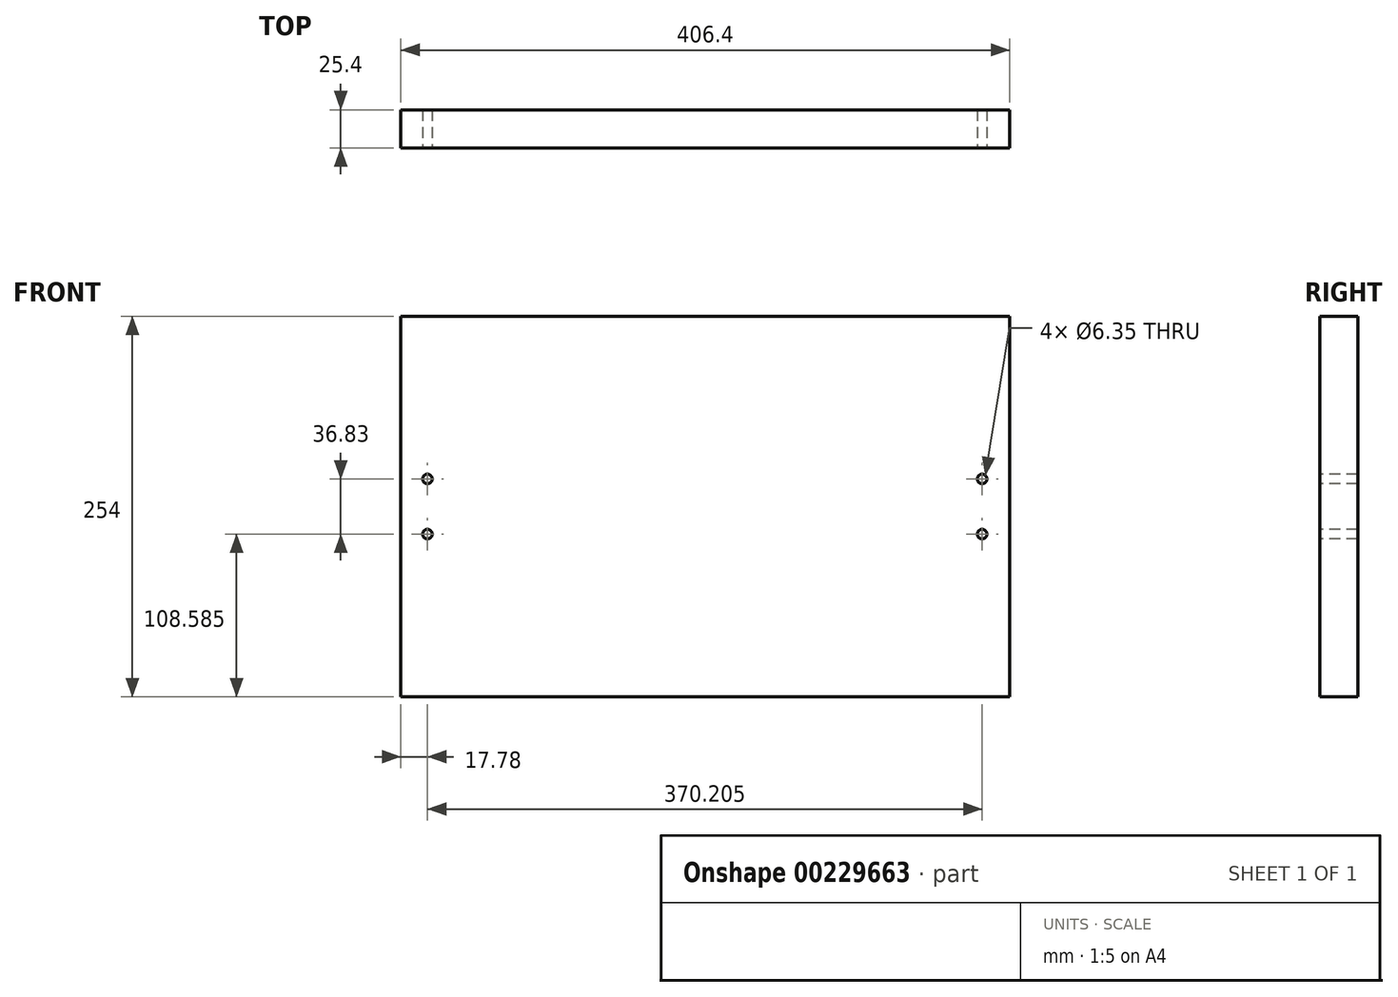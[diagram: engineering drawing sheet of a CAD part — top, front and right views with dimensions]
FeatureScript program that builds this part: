
annotation { "Feature Type Name" : "Feature", "Feature Type Description" : "" }
export const myFeature = defineFeature(function(context is Context, id is Id, definition is map)
    precondition{}
    {
        {
            var Q0;
            Q0=qCreatedBy(makeId("Front.planeOp"),FACE);
            var sketch = newSketch(context, id + "F0", { "sketchPlane" : qUnion([Q0])});
            skLineSegment(sketch, "E0.bottom", {"start": v(0, 0) * mm, "end": v(406.4, 0) * mm});
            skLineSegment(sketch, "E0.top", {"start": v(0, 254) * mm, "end": v(406.4, 254) * mm});
            skLineSegment(sketch, "E0.left", {"start": v(0, 0) * mm, "end": v(0, 254) * mm});
            skLineSegment(sketch, "E0.right", {"start": v(406.4, 0) * mm, "end": v(406.4, 254) * mm});
            skSolve(sketch);
        }
        {
            var Q0;
            Q0 = qSketchRegion(id + "F0", true);
            extrude(context, id + "F1", {"entities" : qUnion([Q0]), "depth" : 25.4 * mm});
        }
        {
            var Q0;
            Q0=makeQuery(id+"F1.opExtrude","CAP_FACE",FACE,{"disambiguationData":[OSD([sQuery(id+"F0.wireOp",EDGE,"E0.bottom"),sQuery(id+"F0.wireOp",EDGE,"E0.top"),sQuery(id+"F0.wireOp",EDGE,"E0.left"),sQuery(id+"F0.wireOp",EDGE,"E0.right")])],"isStart":false});
            var sketch = newSketch(context, id + "F2", { "sketchPlane" : qUnion([Q0])});
            skLineSegment(sketch, "E1", {"start": v(0, 127) * mm, "end": v(406.4, 127) * mm, "construction": true});
            skPoint(sketch, "E2", {"position": v(17.78, 108.59) * mm});
            skPoint(sketch, "E3", {"position": v(17.78, 145.42) * mm});
            skPoint(sketch, "E4", {"position": v(387.98, 145.42) * mm});
            skPoint(sketch, "E5", {"position": v(387.98, 108.59) * mm});
            skSolve(sketch);
        }
        {
            var Q0;
            Q0=sQuery(id+"F2.wireOp",VERTEX,"E3");
            var Q1;
            Q1=sQuery(id+"F2.wireOp",VERTEX,"E2");
            var Q2;
            Q2=sQuery(id+"F2.wireOp",VERTEX,"E4");
            var Q3;
            Q3=sQuery(id+"F2.wireOp",VERTEX,"E5");
            var Q4;
            Q4=makeQuery(id+"F1.opExtrude","SWEPT_BODY",BODY,{"disambiguationData":[OSD([sQuery(id+"F0.wireOp",EDGE,"E0.bottom"),sQuery(id+"F0.wireOp",EDGE,"E0.top"),sQuery(id+"F0.wireOp",EDGE,"E0.left"),sQuery(id+"F0.wireOp",EDGE,"E0.right")])]});
            hole(context, id + "F3", {"style" : HoleStyle.SIMPLE, "endStyle" : HoleEndStyle.THROUGH, "holeDiameter" : 6.35 * mm, "locations" : qUnion([Q0, Q1, Q2, Q3]), "scope" : qUnion([Q4]), "isTappedThrough" : true});
        }
    });
